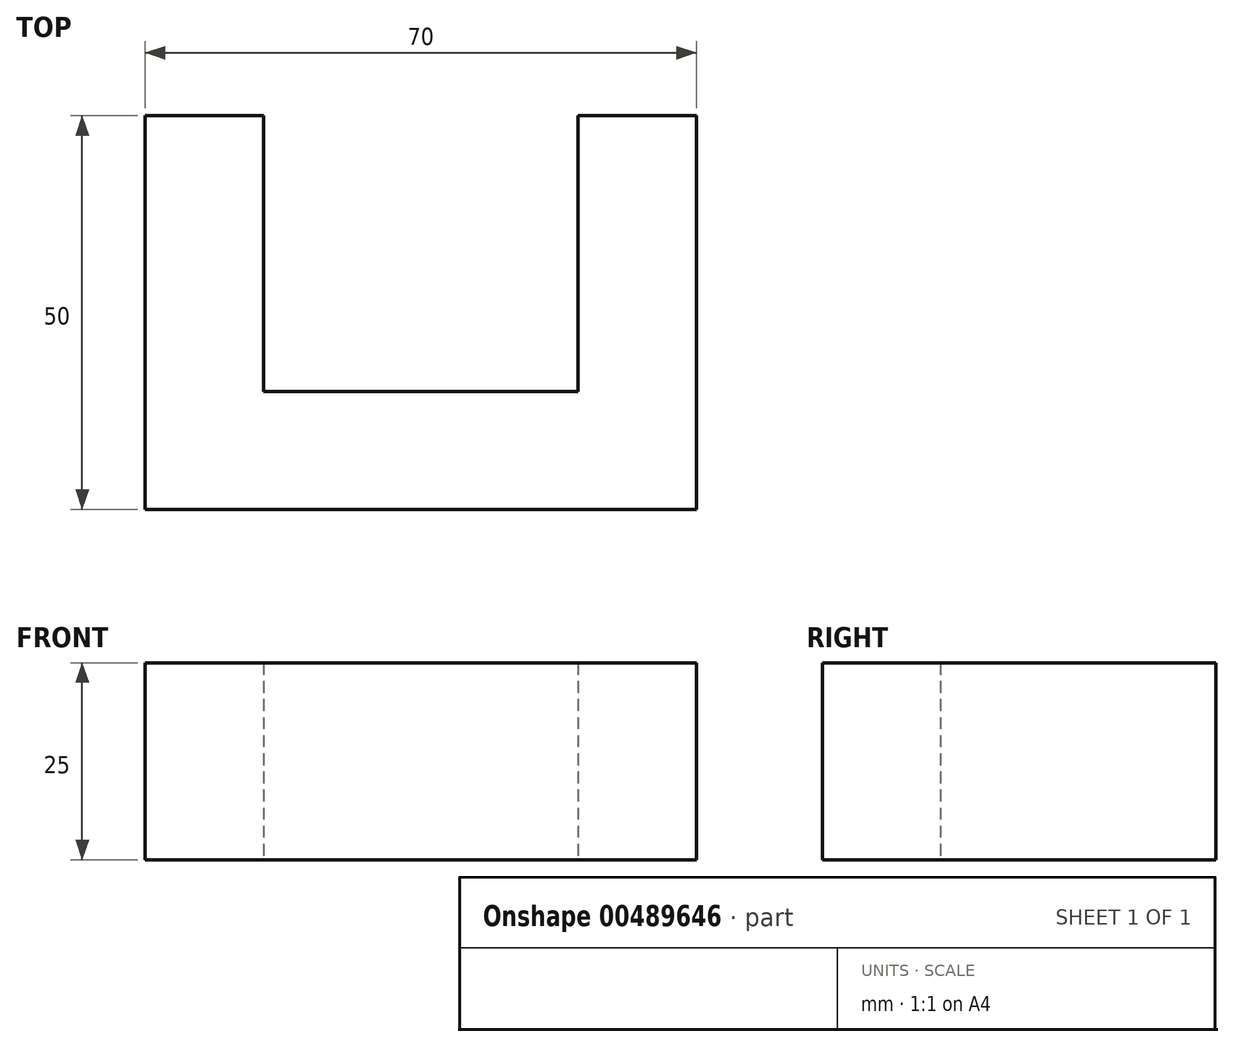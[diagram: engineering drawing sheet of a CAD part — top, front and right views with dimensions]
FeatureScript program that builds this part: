
annotation { "Feature Type Name" : "Feature", "Feature Type Description" : "" }
export const myFeature = defineFeature(function(context is Context, id is Id, definition is map)
    precondition{}
    {
        {
            var Q0;
            Q0=qCreatedBy(makeId("Top.planeOp"),FACE);
            var sketch = newSketch(context, id + "F0", { "sketchPlane" : qUnion([Q0])});
            skLineSegment(sketch, "E0", {"start": v(0, 0) * mm, "end": v(70, 0) * mm});
            skLineSegment(sketch, "E1", {"start": v(70, 0) * mm, "end": v(70, 50) * mm});
            skLineSegment(sketch, "E2", {"start": v(70, 50) * mm, "end": v(55, 50) * mm});
            skLineSegment(sketch, "E3", {"start": v(55, 50) * mm, "end": v(55, 15) * mm});
            skLineSegment(sketch, "E4", {"start": v(55, 15) * mm, "end": v(15, 15) * mm});
            skLineSegment(sketch, "E5", {"start": v(15, 50) * mm, "end": v(0, 50) * mm});
            skLineSegment(sketch, "E6", {"start": v(0, 50) * mm, "end": v(0, 0) * mm});
            skLineSegment(sketch, "E7", {"start": v(15, 50) * mm, "end": v(15, 15) * mm});
            skLineSegment(sketch, "E8", {"start": v(15, 15) * mm, "end": v(15, 0) * mm, "construction": true});
            skSolve(sketch);
        }
        {
            var Q0;
            Q0=makeQuery(id+"F0.imprint","IMPRINT",FACE,{"disambiguationData":[TD([[makeQuery(id+"F0.imprint","IMPRINT",EDGE,{"derivedFrom":sQuery(id+"F0.wireOp",EDGE,"E0")}),1.0]])]});
            extrude(context, id + "F1", {"entities" : qUnion([Q0]), "depth" : 25 * mm});
        }
    });
